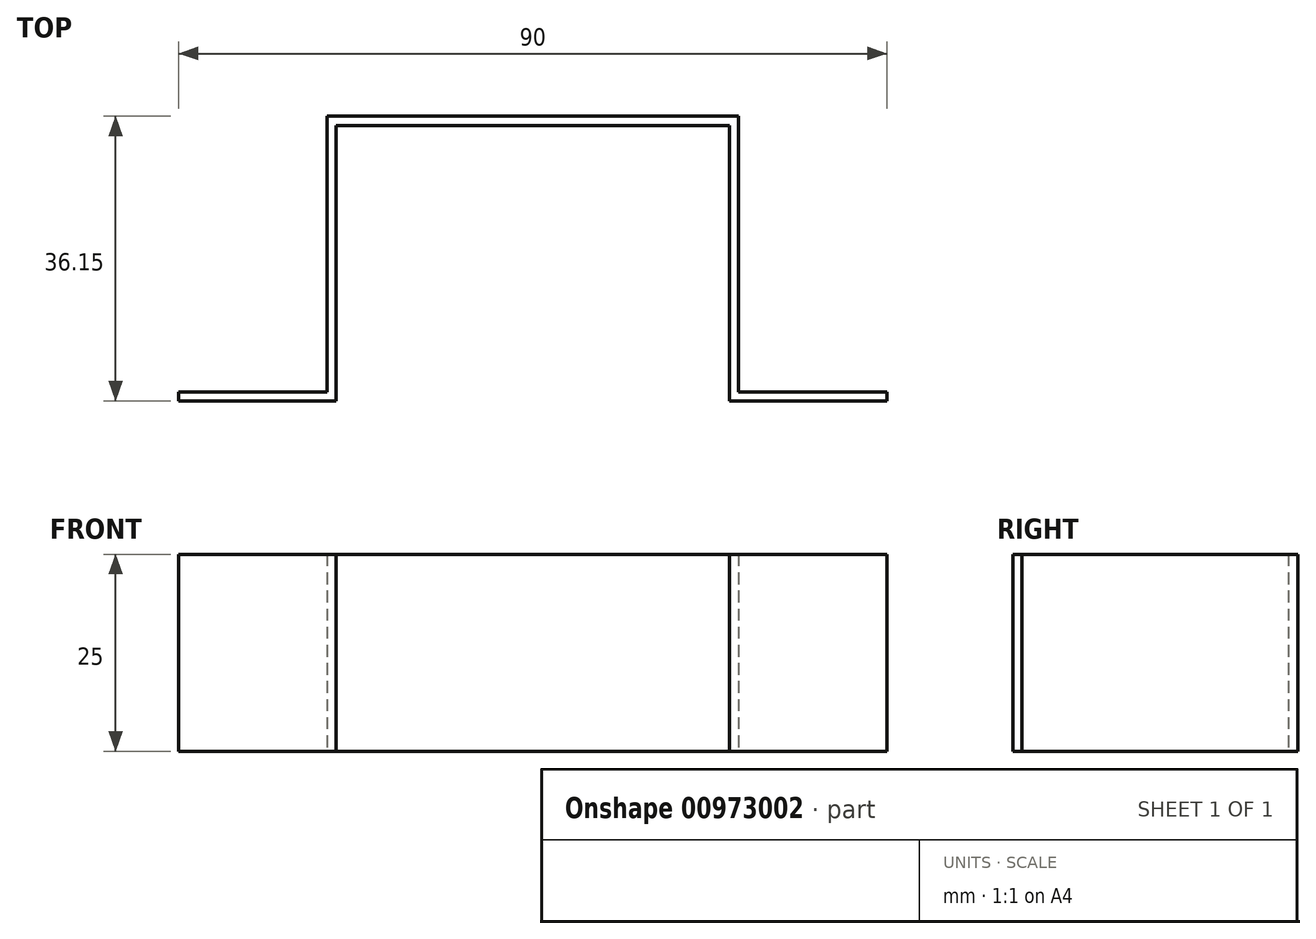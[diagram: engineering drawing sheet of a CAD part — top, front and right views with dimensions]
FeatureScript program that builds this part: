
annotation { "Feature Type Name" : "Feature", "Feature Type Description" : "" }
export const myFeature = defineFeature(function(context is Context, id is Id, definition is map)
    precondition{}
    {
        {
            var Q0;
            Q0=qCreatedBy(makeId("Top.planeOp"),FACE);
            var sketch = newSketch(context, id + "F0", { "sketchPlane" : qUnion([Q0])});
            skLineSegment(sketch, "E0", {"start": v(-39.5, 0) * mm, "end": v(-19.5, 0) * mm});
            skLineSegment(sketch, "E1", {"start": v(-19.5, 0) * mm, "end": v(-19.5, 35) * mm});
            skLineSegment(sketch, "E2", {"start": v(-19.5, 35) * mm, "end": v(30.5, 35) * mm});
            skLineSegment(sketch, "E3", {"start": v(30.5, 35) * mm, "end": v(30.5, 0) * mm});
            skLineSegment(sketch, "E4", {"start": v(30.5, 0) * mm, "end": v(50.5, 0) * mm});
            skLineSegment(sketch, "E5.0", {"start": v(31.65, 1.15) * mm, "end": v(50.5, 1.15) * mm});
            skLineSegment(sketch, "E5.1", {"start": v(-39.5, 1.15) * mm, "end": v(-20.65, 1.15) * mm});
            skLineSegment(sketch, "E5.2", {"start": v(-20.65, 1.15) * mm, "end": v(-20.65, 36.15) * mm});
            skLineSegment(sketch, "E5.3", {"start": v(-20.65, 36.15) * mm, "end": v(31.65, 36.15) * mm});
            skLineSegment(sketch, "E5.4", {"start": v(31.65, 36.15) * mm, "end": v(31.65, 1.15) * mm});
            skLineSegment(sketch, "E6", {"start": v(-39.5, 1.15) * mm, "end": v(-39.5, 0) * mm});
            skLineSegment(sketch, "E7", {"start": v(50.5, 1.15) * mm, "end": v(50.5, 0) * mm});
            skSolve(sketch);
        }
        {
            var Q0;
            Q0 = qSketchRegion(id + "F0", true);
            extrude(context, id + "F1", {"entities" : qUnion([Q0]), "depth" : 25 * mm, "offsetDistance" : 25 * mm});
        }
    });
